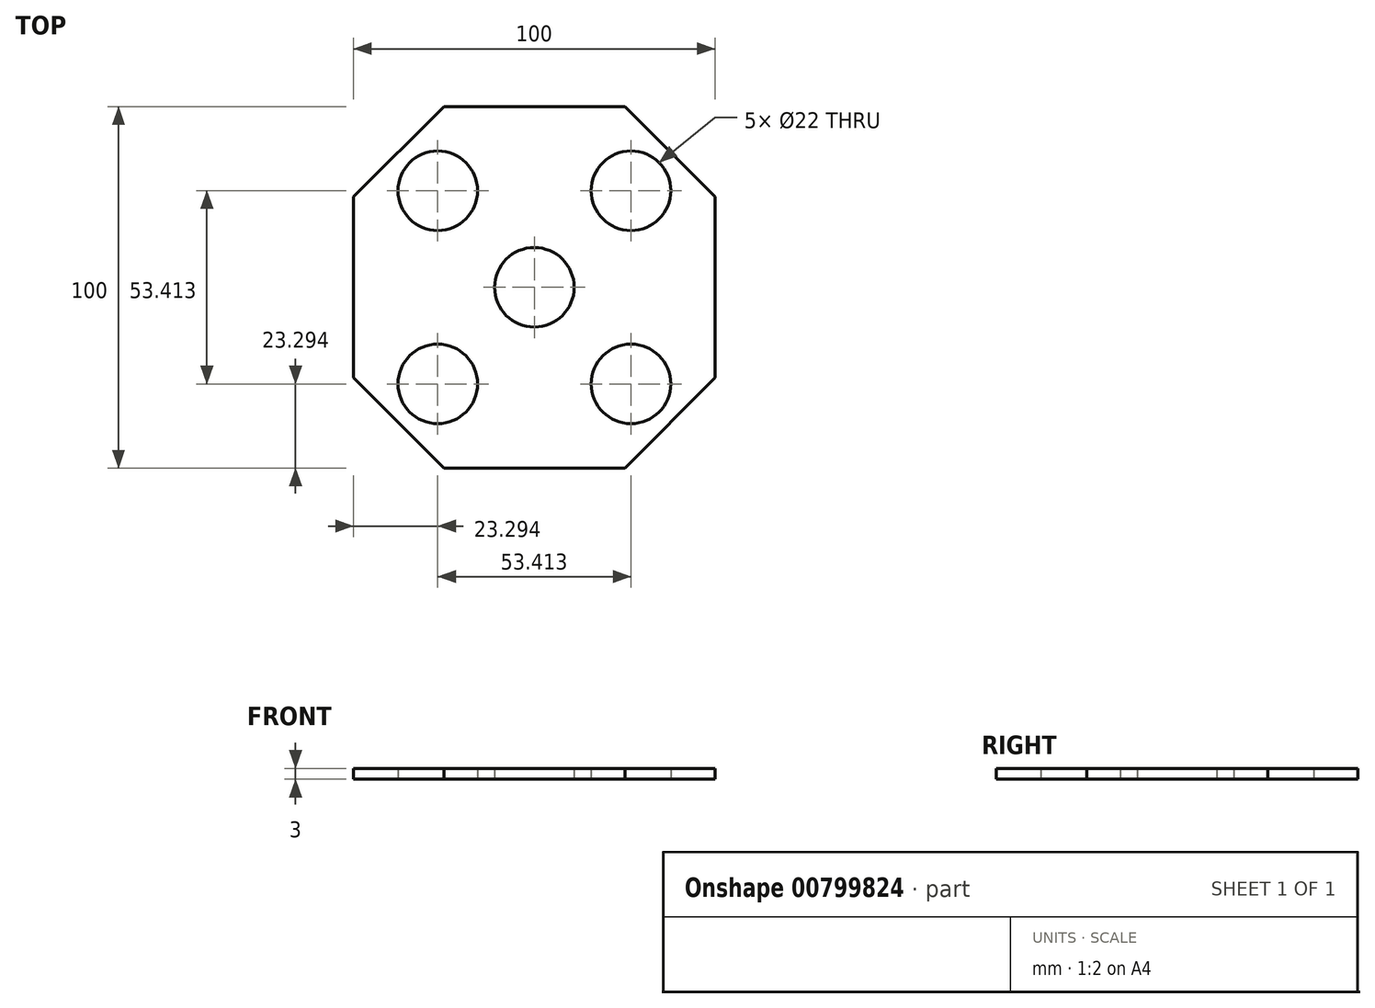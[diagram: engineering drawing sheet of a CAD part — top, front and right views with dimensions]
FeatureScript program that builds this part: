
annotation { "Feature Type Name" : "Feature", "Feature Type Description" : "" }
export const myFeature = defineFeature(function(context is Context, id is Id, definition is map)
    precondition{}
    {
        {
            var Q0;
            Q0=qCreatedBy(makeId("Top.planeOp"),FACE);
            var sketch = newSketch(context, id + "F0", { "sketchPlane" : qUnion([Q0])});
            skCircle(sketch, "E0", {"center": v(0, 0) * mm, "radius": 11 * mm});
            skLineSegment(sketch, "E1", {"start": v(0, 50) * mm, "end": v(-25, 50) * mm});
            skLineSegment(sketch, "E2", {"start": v(-50, 0) * mm, "end": v(-50, 25) * mm});
            skLineSegment(sketch, "E3", {"start": v(-50, 25) * mm, "end": v(-25, 50) * mm});
            skCircle(sketch, "E4", {"center": v(-26.7, 26.7) * mm, "radius": 11 * mm});
            skCircle(sketch, "E5.1.1", {"center": v(-26.7, -26.7) * mm, "radius": 11 * mm});
            skLineSegment(sketch, "E5.1.3", {"start": v(-50, 0) * mm, "end": v(-50, -25) * mm});
            skLineSegment(sketch, "E5.1.5", {"start": v(-25, -50) * mm, "end": v(-50, -25) * mm});
            skLineSegment(sketch, "E5.1.6", {"start": v(0, -50) * mm, "end": v(-25, -50) * mm});
            skCircle(sketch, "E5.2.1", {"center": v(26.7, -26.7) * mm, "radius": 11 * mm});
            skLineSegment(sketch, "E5.2.3", {"start": v(0, -50) * mm, "end": v(25, -50) * mm});
            skLineSegment(sketch, "E5.2.5", {"start": v(50, -25) * mm, "end": v(25, -50) * mm});
            skLineSegment(sketch, "E5.2.6", {"start": v(50, 0) * mm, "end": v(50, -25) * mm});
            skCircle(sketch, "E5.3.1", {"center": v(26.7, 26.7) * mm, "radius": 11 * mm});
            skLineSegment(sketch, "E5.3.3", {"start": v(50, 0) * mm, "end": v(50, 25) * mm});
            skLineSegment(sketch, "E5.3.5", {"start": v(25, 50) * mm, "end": v(50, 25) * mm});
            skLineSegment(sketch, "E5.3.6", {"start": v(0, 50) * mm, "end": v(25, 50) * mm});
            skSolve(sketch);
        }
        {
            var Q0;
            Q0=makeQuery(id+"F0.imprint","IMPRINT",FACE,{"disambiguationData":[TD([[makeQuery(id+"F0.imprint","IMPRINT",EDGE,{"derivedFrom":sQuery(id+"F0.wireOp",EDGE,"E1")}),1.0]])]});
            extrude(context, id + "F1", {"entities" : qUnion([Q0]), "depth" : 3 * mm, "offsetDistance" : 25 * mm});
        }
    });
